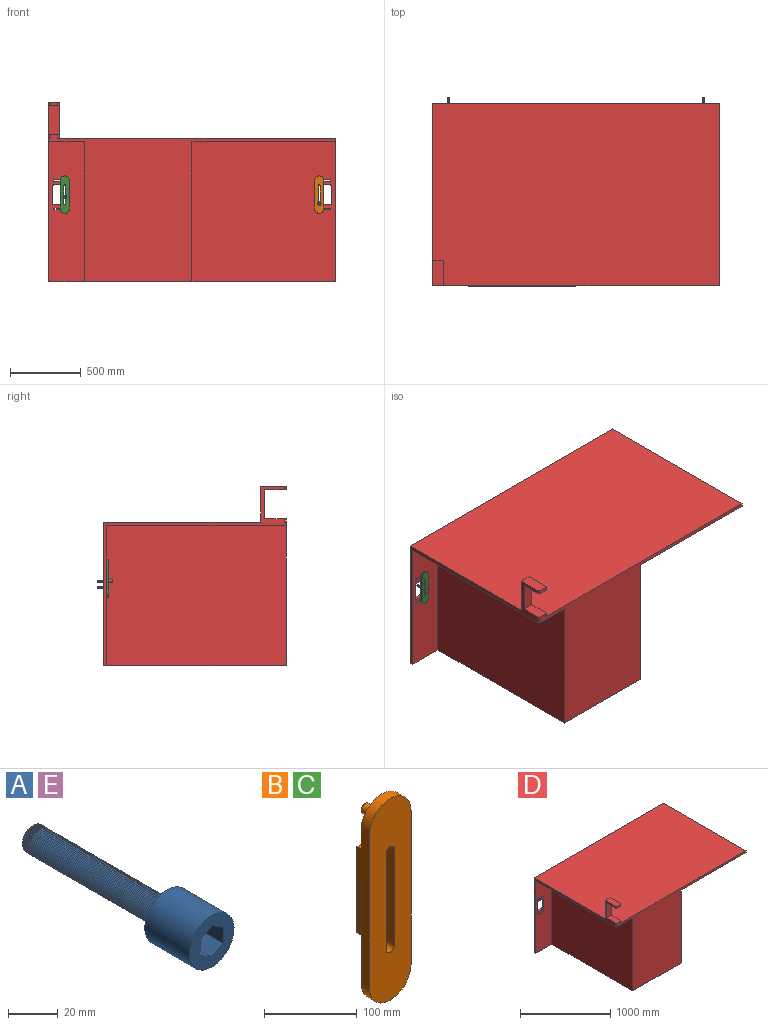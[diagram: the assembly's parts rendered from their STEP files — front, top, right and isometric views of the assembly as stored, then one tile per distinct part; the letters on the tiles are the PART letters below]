
ASSEMBLY  parts=5 mates=4
PART A: 20 faces, bbox 26.1x102.9x26.1 mm
  f0: plane 25.4x25.4mm, normal (0,1,0), area 380mm2, adj f1,f3,f11
  f1: cylinder r=6.35mm len=12.7mm, axis (0,1,0), area 5.8mm2, adj f0,f12,f13
  f2: plane 25.4x25.4mm, normal (0,-1,0), area 355.9mm2, adj f3,f4,f5,f6,f7,f8,f9
  f3: cylinder r=12.7mm len=25.4mm, axis (0,1,0), area 2026.8mm2, adj f0,f2
  f4: plane 15.24x6.44mm, normal (-0.54,0,-0.84), area 116.1mm2, adj f2,f5,f9,f10
  f5: plane 15.24x6.75mm, normal (0.46,0,-0.89), area 116.1mm2, adj f2,f4,f6,f10
  f6: plane 15.24x7.61mm, normal (1,0,-0.04), area 116.1mm2, adj f2,f5,f7,f10
  f7: plane 15.24x6.44mm, normal (0.54,0,0.84), area 116.1mm2, adj f2,f6,f8,f10
  f8: plane 15.24x6.75mm, normal (-0.46,0,0.89), area 116.1mm2, adj f2,f7,f9,f10
  f9: plane 15.24x7.61mm, normal (-1,0,0.04), area 116.1mm2, adj f2,f4,f8,f10
  f10: plane 15.23x13.5mm, normal (0,-1,0), area 150.9mm2, adj f4,f5,f6,f7,f8,f9
  f11: cylinder r=6.35mm len=12.37mm, axis (0,1,0), area 3.9mm2, adj f0,f12,f13
  f12: plane 0.98x0.88mm, normal (0,0,1), area 0.4mm2, adj f1,f11,f13,f15,f16
  f13: bspline ~14.67x12.7mm, area 2.5mm2, adj f1,f11,f12,f15
  f14: plane 0.74x0.4mm, normal (0,0,-1), area 0.2mm2, adj f15,f17,f18,f19
  f15: bspline ~76.68x14.54mm, area 2813mm2, adj f12,f13,f14,f16,f18
  f16: bspline ~76.68x14.54mm, area 2788.6mm2, adj f12,f15,f17,f18
  f17: bspline ~12.7x7.33mm, area 1mm2, adj f14,f16,f18,f19
  f18: plane 13.22x12.8mm, normal (0,1,0), area 115.2mm2, adj f14,f15,f16,f17,f19
  f19: cylinder r=6.35mm len=11.11mm, axis (0,1,0), area 2.8mm2, adj f14,f17,f18
PART B: 22 faces, bbox 63.5x38.1x266.7 mm
  f0: cylinder r=31.75mm len=63.5mm, axis (0,1,0), area 1266.8mm2, adj f1,f7,f8,f9
  f1: plane 203.2x12.7mm, normal (-1,0,0), area 2580.6mm2, adj f0,f2,f8,f9
  f2: cylinder r=31.75mm len=63.5mm, axis (0,1,0), area 1266.8mm2, adj f1,f7,f8,f9
  f3: cylinder r=6.35mm len=12.7mm, axis (0,1,0), area 253.4mm2, adj f4,f6,f8,f9
  f4: plane 127x38.1mm, normal (-1,0,0), area 4516.1mm2, adj f3,f5,f8,f9,f14,f16,f17
  f5: cylinder r=6.35mm len=12.7mm, axis (0,1,0), area 253.4mm2, adj f4,f6,f8,f9
  f6: plane 127x38.1mm, normal (1,0,0), area 4516.1mm2, adj f3,f5,f8,f9,f10,f11,f13
  f7: plane 203.2x12.7mm, normal (1,0,0), area 2580.6mm2, adj f0,f2,f8,f9
  f8: plane 266.7x63.5mm, normal (0,-1,0), area 14330.5mm2, adj f0,f1,f2,f3,f4,f5,f6,f7
  f9: plane 266.7x63.5mm, normal (0,1,0), area 12625.6mm2, adj f0,f1,f2,f3,f4,f5,f6,f7
  f10: plane 25.4x6.35mm, normal (0,0,1), area 161.3mm2, adj f6,f9,f12,f13
  f11: plane 25.4x6.35mm, normal (0,0,-1), area 161.3mm2, adj f6,f9,f12,f13
  f12: plane 114.3x25.4mm, normal (-1,0,0), area 2903.2mm2, adj f9,f10,f11,f13
  f13: plane 114.3x6.35mm, normal (0,1,0), area 725.8mm2, adj f6,f10,f11,f12
  f14: plane 25.4x6.35mm, normal (0,0,1), area 161.3mm2, adj f4,f9,f15,f17
  f15: plane 114.3x25.4mm, normal (1,0,0), area 2903.2mm2, adj f9,f14,f16,f17
  f16: plane 25.4x6.35mm, normal (0,0,-1), area 161.3mm2, adj f4,f9,f15,f17
  f17: plane 114.3x6.35mm, normal (0,1,0), area 725.8mm2, adj f4,f14,f15,f16
  f18: cylinder r=6.35mm len=25.4mm, axis (0,1,0), area 1013.4mm2, adj f9,f19
  f19: plane 12.7x12.7mm, normal (0,1,0), area 126.7mm2, adj f18
  f20: cylinder r=6.35mm len=25.4mm, axis (0,1,0), area 1013.4mm2, adj f9,f21
  f21: plane 12.7x12.7mm, normal (0,1,0), area 126.7mm2, adj f20
PART C: same geometry as B
PART D: 56 faces, bbox 2032x1295.4x1270 mm
  f0: plane 2032x1041.4mm, normal (0,-1,0), area 807740.3mm2, adj f1,f5,f8,f9,f11,f12,f14,f47
  f1: plane 1295.4x1270mm, normal (-1,0,0), area 71612.8mm2, adj f0,f2,f5,f7,f10,f11,f12,f48
  f2: cylinder r=12.7mm len=25.4mm, axis (0,0,-1), area 506.7mm2, adj f1,f13,f52,f53
  f3: cylinder r=12.7mm len=25.4mm, axis (0,0,-1), area 506.7mm2, adj f4,f13,f52,f53
  f4: plane 254x165.1mm, normal (1,0,0), area 13548.4mm2, adj f3,f5,f50,f51,f52,f53,f54,f55
  f5: plane 2032x1295.4mm, normal (0,0,1), area 2618739.1mm2, adj f0,f1,f4,f10,f14,f50,f51
  f6: plane 1016x990.6mm, normal (0,-1,0), area 990205.7mm2, adj f9,f12,f14,f31,f32,f33,f34,f35
  f7: plane 990.6x254mm, normal (0,-1,0), area 235368.5mm2, adj f1,f8,f12,f15,f16,f17,f18,f19
  f8: plane 1270x990.6mm, normal (-1,0,0), area 1258062mm2, adj f0,f7,f12,f48
  f9: plane 1270x990.6mm, normal (1,0,0), area 1258062mm2, adj f0,f6,f12,f47
  f10: plane 2032x1016mm, normal (0,1,0), area 2032024.2mm2, adj f1,f5,f12,f14,f15,f16,f17,f18
  f11: plane 12.7x12.7mm, normal (0,0,1), area 34.6mm2, adj f0,f1,f49
  f12: plane 2032x1295.4mm, normal (0,0,-1), area 1019352.8mm2, adj f0,f1,f6,f7,f8,f9,f10,f14
  f13: plane 50.8x25.4mm, normal (0,-1,0), area 1290.3mm2, adj f2,f3,f52,f53
  f14: plane 1295.4x1016mm, normal (1,0,0), area 58064.4mm2, adj f0,f5,f6,f10,f12,f47
  f15: cylinder r=6.35mm len=25.4mm, axis (0,-1,0), area 506.7mm2, adj f7,f10,f16,f18
  f16: plane 76.2x25.4mm, normal (0,0,1), area 1935.5mm2, adj f7,f10,f15,f17
  f17: cylinder r=6.35mm len=25.4mm, axis (0,-1,0), area 506.7mm2, adj f7,f10,f16,f18
  f18: plane 76.2x25.4mm, normal (0,0,-1), area 1935.5mm2, adj f7,f10,f15,f17
  f19: cylinder r=6.35mm len=25.4mm, axis (0,-1,0), area 506.7mm2, adj f7,f10,f20,f22
  f20: plane 76.2x25.4mm, normal (0,0,1), area 1935.5mm2, adj f7,f10,f19,f21
  f21: cylinder r=6.35mm len=25.4mm, axis (0,-1,0), area 506.7mm2, adj f7,f10,f20,f22
  f22: plane 76.2x25.4mm, normal (0,0,-1), area 1935.5mm2, adj f7,f10,f19,f21
  f23: plane 114.3x25.4mm, normal (-1,0,0), area 2903.2mm2, adj f7,f10,f24,f30
  f24: cylinder r=12.7mm len=25.4mm, axis (0,-1,0), area 506.7mm2, adj f7,f10,f23,f25
  f25: plane 76.2x25.4mm, normal (0,0,-1), area 1935.5mm2, adj f7,f10,f24,f26
  f26: cylinder r=12.7mm len=25.4mm, axis (0,-1,0), area 506.7mm2, adj f7,f10,f25,f27
  f27: plane 114.3x25.4mm, normal (1,0,0), area 2903.2mm2, adj f7,f10,f26,f28
  f28: cylinder r=12.7mm len=25.4mm, axis (0,-1,0), area 506.7mm2, adj f7,f10,f27,f29
  f29: plane 76.2x25.4mm, normal (0,0,1), area 1935.5mm2, adj f7,f10,f28,f30
  f30: cylinder r=12.7mm len=25.4mm, axis (0,-1,0), area 506.7mm2, adj f7,f10,f23,f29
  f31: plane 114.3x25.4mm, normal (-1,0,0), area 2903.2mm2, adj f6,f10,f32,f38
  f32: cylinder r=12.7mm len=25.4mm, axis (0,-1,0), area 506.7mm2, adj f6,f10,f31,f33
  f33: plane 76.2x25.4mm, normal (0,0,-1), area 1935.5mm2, adj f6,f10,f32,f34
  f34: cylinder r=12.7mm len=25.4mm, axis (0,-1,0), area 506.7mm2, adj f6,f10,f33,f35
  f35: plane 114.3x25.4mm, normal (1,0,0), area 2903.2mm2, adj f6,f10,f34,f36
  f36: cylinder r=12.7mm len=25.4mm, axis (0,-1,0), area 506.7mm2, adj f6,f10,f35,f37
  f37: plane 76.2x25.4mm, normal (0,0,1), area 1935.5mm2, adj f6,f10,f36,f38
  f38: cylinder r=12.7mm len=25.4mm, axis (0,-1,0), area 506.7mm2, adj f6,f10,f31,f37
  f39: cylinder r=6.35mm len=25.4mm, axis (0,-1,0), area 506.7mm2, adj f6,f10,f40,f42
  f40: plane 76.2x25.4mm, normal (0,0,1), area 1935.5mm2, adj f6,f10,f39,f41
  f41: cylinder r=6.35mm len=25.4mm, axis (0,-1,0), area 506.7mm2, adj f6,f10,f40,f42
  f42: plane 76.2x25.4mm, normal (0,0,-1), area 1935.5mm2, adj f6,f10,f39,f41
  f43: cylinder r=6.35mm len=25.4mm, axis (0,-1,0), area 506.7mm2, adj f6,f10,f44,f46
  f44: plane 76.2x25.4mm, normal (0,0,1), area 1935.5mm2, adj f6,f10,f43,f45
  f45: cylinder r=6.35mm len=25.4mm, axis (0,-1,0), area 506.7mm2, adj f6,f10,f44,f46
  f46: plane 76.2x25.4mm, normal (0,0,-1), area 1935.5mm2, adj f6,f10,f43,f45
  f47: plane 1270x1016mm, normal (0,0,-1), area 1290320mm2, adj f0,f6,f9,f14
  f48: plane 1270x254mm, normal (0,0,-1), area 322580mm2, adj f0,f1,f7,f8
  f49: cylinder r=12.7mm len=25.4mm, axis (0,0,-1), area 506.7mm2, adj f0,f1,f11,f54
  f50: cylinder r=12.7mm len=25.4mm, axis (0,0,-1), area 506.7mm2, adj f0,f4,f5,f54
  f51: plane 254x76.2mm, normal (0,1,0), area 19354.8mm2, adj f1,f4,f5,f52
  f52: plane 177.8x76.2mm, normal (0,0,1), area 13479.1mm2, adj f1,f2,f3,f4,f13,f51
  f53: plane 152.4x76.2mm, normal (0,0,-1), area 11543.7mm2, adj f1,f2,f3,f4,f13,f55
  f54: plane 152.4x76.2mm, normal (0,0,1), area 11543.7mm2, adj f0,f1,f4,f49,f50,f55
  f55: plane 203.2x76.2mm, normal (0,-1,0), area 15483.8mm2, adj f1,f4,f53,f54
PART E: same geometry as A
PLACE A rot(axis=(0,-1,0),61.8deg) t=(6.82,155.71,1453.67)mm
PLACE B t=(1.95,117.61,1616.08)mm
PLACE C t=(-1801.45,117.61,1616.08)mm
PLACE D t=(-895.82,92.21,777.83)mm fixed
PLACE E rot(axis=(0,-1,0),90deg) t=(-1785.99,155.71,1502.97)mm
MATE pin_slot E.f1 <-> C.f5  axis (0,1,0) through (-1797.52,79.51,1522.45)mm
MATE pin_slot C.f0 <-> D.f19  axis (0,1,0) through (-1797.52,117.61,1641.38)mm
MATE pin_slot B.f0 <-> D.f43  axis (0,1,0) through (5.88,117.61,1641.38)mm
MATE pin_slot A.f1 <-> B.f5  axis (0,1,0) through (5.88,79.51,1476.28)mm
